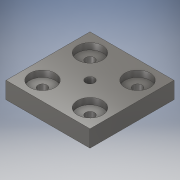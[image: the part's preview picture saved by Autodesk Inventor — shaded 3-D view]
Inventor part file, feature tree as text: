
AUTODESK INVENTOR PART (.ipt)
format: ipt  version: 2018 (Build 220112000, 112)  size: 138,240 bytes
history: native  units: in
note: dims shown in document units (in); Inventor stores cm internally (conversion verified against a paired STEP export)
features: sketch x3, hole x2, extrude x1
ambient origin geometry x8: Origin, YZ Plane, XZ Plane, XY Plane, X Axis, Y Axis, Z Axis, Center Point
bodies: Solid1 (feature_tree)
feature tree (6):
  extrude  "Extrusion1"  Depth=2.5in
  hole  "Hole1"  [1 undecoded]
  hole  "Hole2"  [1 undecoded]
  sketch  "Sketch1"  dims[d0=2.5in d1=2.5in]
  sketch  "Sketch2"  dims[d2=0.5in d3=0.0in d4=1.0in]
  sketch  "Sketch3"  dims[d5=45.0deg d6=1.5748in d8=360.0deg d10=0.266in d11=0.75in d12=0.75in d13=0.188in d14=0.5635in d15=1.0in d16=0.8108in d17=1.0in d18=0.266in d19=0.75in d20=0.75in d21=0.188in d22=0.5635in d23=1.0in d24=0.8108in]
note: 2 required parameter values undecoded (feature->parameter linkage not recoverable at this tier; creation-order binding heuristic only, values carry confidence <= 0.55)
